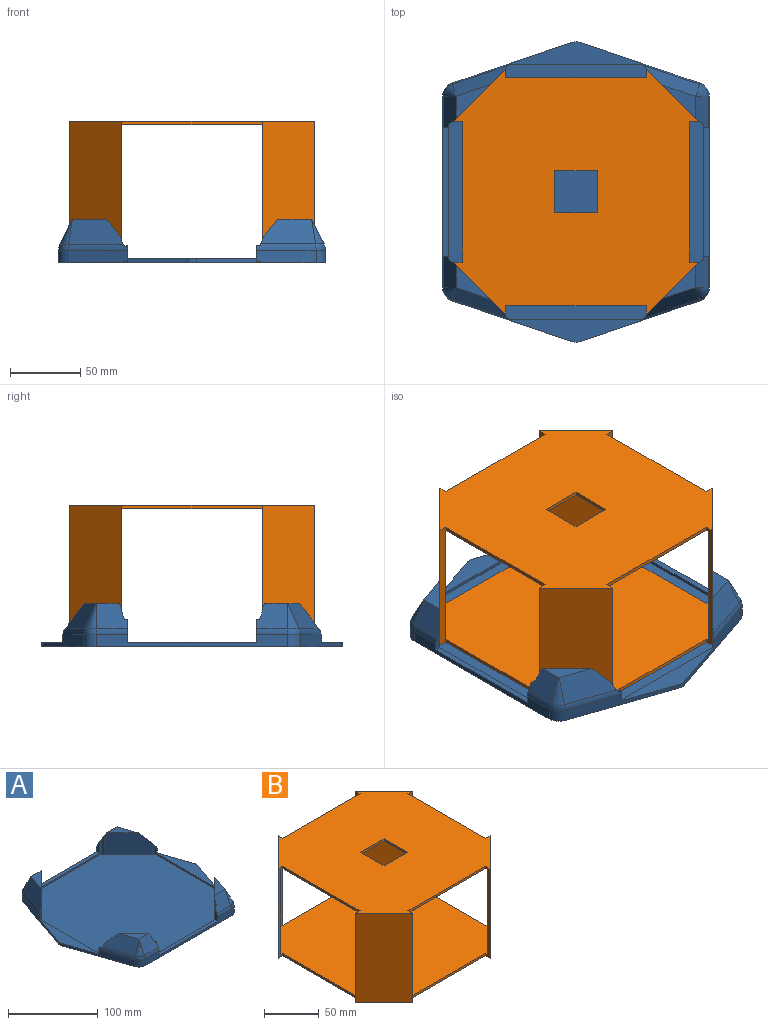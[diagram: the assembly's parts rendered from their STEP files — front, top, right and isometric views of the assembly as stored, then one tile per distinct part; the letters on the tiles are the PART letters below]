
ASSEMBLY  parts=2 mates=1
PART A: 70 faces, bbox 213.9x190x31 mm
  f0: plane 182x182mm, normal (0,0,1), area 29110.5mm2, adj f20,f21,f22,f23,f24,f25,f26,f27
  f1: plane 85x29.08mm, normal (-0.95,0.32,0), area 531.7mm2, adj f7,f14,f35,f40,f45,f67
  f2: plane 135.7x8.69mm, normal (0,1,0), area 672.4mm2, adj f7,f15,f17,f37,f40,f41,f66,f69
  f3: plane 85x29.08mm, normal (0.95,0.32,0), area 531.7mm2, adj f7,f18,f39,f41,f42,f64
  f4: plane 85x29.08mm, normal (0.95,-0.32,0), area 544.3mm2, adj f7,f11,f39,f42,f43,f63
  f5: plane 135.7x8.97mm, normal (0,-1,0), area 684.7mm2, adj f7,f8,f12,f33,f43,f44,f60,f61
  f6: plane 85x29.08mm, normal (-0.95,-0.32,0), area 544.3mm2, adj f7,f9,f35,f44,f45,f58
  f7: plane 213.86x190mm, normal (0,0,-1), area 34634.8mm2, adj f1,f2,f3,f4,f5,f6,f40,f41
  f8: plane 16.04x4mm, normal (1,0,0), area 48mm2, adj f5,f28,f33,f54,f60
  f9: plane 9.52x0.76mm, normal (0,1,0), area 6.3mm2, adj f6,f26,f35,f58
  f10: plane 24.1x24.1mm, normal (0,0,1), area 191mm2, adj f27,f52,f54
  f11: plane 9.52x0.76mm, normal (0,1,0), area 6.3mm2, adj f4,f31,f39,f63
  f12: plane 16.04x4mm, normal (-1,0,0), area 48mm2, adj f5,f29,f33,f57,f61
  f13: plane 24.1x24.1mm, normal (0,0,1), area 191mm2, adj f30,f55,f57
  f14: plane 9.24x0.76mm, normal (0,-1,0), area 6.1mm2, adj f1,f25,f35,f67
  f15: plane 16.02x4mm, normal (1,0,0), area 47.3mm2, adj f2,f23,f37,f46,f69
  f16: plane 24.73x24.73mm, normal (0,0,1), area 201.2mm2, adj f24,f46,f47,f48
  f17: plane 16.02x4mm, normal (-1,0,0), area 47.3mm2, adj f2,f22,f37,f49,f66
  f18: plane 9.24x0.76mm, normal (0,-1,0), area 6.1mm2, adj f3,f20,f39,f64
  f19: plane 24.73x24.73mm, normal (0,0,1), area 201.2mm2, adj f21,f49,f50,f51
  f20: cylinder r=4mm len=16.59mm, axis (0,0,1), area 78.8mm2, adj f0,f18,f21,f38,f51,f64
  f21: plane 37x37mm, normal (-0.71,-0.71,0), area 1465.6mm2, adj f0,f19,f20,f22,f49,f51
  f22: cylinder r=4mm len=26.4mm, axis (0,0,1), area 133.1mm2, adj f0,f17,f21,f36,f49
  f23: cylinder r=4mm len=26.4mm, axis (0,0,1), area 133.1mm2, adj f0,f15,f24,f36,f46
  f24: plane 37x37mm, normal (0.71,-0.71,0), area 1465.6mm2, adj f0,f16,f23,f25,f46,f48
  f25: cylinder r=4mm len=16.59mm, axis (0,0,1), area 78.8mm2, adj f0,f14,f24,f34,f48,f67
  f26: cylinder r=4mm len=16.68mm, axis (0,0,1), area 80.4mm2, adj f0,f9,f27,f34,f52,f58
  f27: plane 37x37mm, normal (0.71,0.71,0), area 1461.5mm2, adj f0,f10,f26,f28,f52,f54
  f28: cylinder r=4mm len=26.07mm, axis (0,0,1), area 132.4mm2, adj f0,f8,f27,f32,f54
  f29: cylinder r=4mm len=26.07mm, axis (0,0,1), area 132.4mm2, adj f0,f12,f30,f32,f57
  f30: plane 37x37mm, normal (-0.71,0.71,0), area 1461.5mm2, adj f0,f13,f29,f31,f55,f57
  f31: cylinder r=4mm len=16.68mm, axis (0,0,1), area 80.4mm2, adj f0,f11,f30,f38,f55,f63
  f32: plane 92x2.18mm, normal (0,1,0), area 200.6mm2, adj f0,f28,f29,f33
  f33: plane 92x4mm, normal (0,0,1), area 368mm2, adj f5,f8,f12,f32
  f34: plane 92x2.18mm, normal (1,0,0), area 200.6mm2, adj f0,f25,f26,f35
  f35: plane 92x15.93mm, normal (0,0,1), area 792.9mm2, adj f1,f6,f9,f14,f34,f45
  f36: plane 92x2.18mm, normal (0,-1,0), area 200.6mm2, adj f0,f22,f23,f37
  f37: plane 92x4mm, normal (0,0,1), area 368mm2, adj f2,f15,f17,f36
  f38: plane 92x2.18mm, normal (-1,0,0), area 200.6mm2, adj f0,f20,f31,f39
  f39: plane 92x15.93mm, normal (0,0,1), area 792.9mm2, adj f3,f4,f11,f18,f38,f42
  f40: cylinder r=10mm len=9.46mm, axis (0,0,-1), area 107.9mm2, adj f1,f2,f7,f68
  f41: cylinder r=10mm len=9.46mm, axis (0,0,-1), area 107.9mm2, adj f2,f3,f7,f65
  f42: cylinder r=10mm len=6.47mm, axis (0,0,1), area 21mm2, adj f3,f4,f7,f39
  f43: cylinder r=10mm len=9.46mm, axis (0,0,-1), area 111.4mm2, adj f4,f5,f7,f62
  f44: cylinder r=10mm len=9.46mm, axis (0,0,-1), area 111.4mm2, adj f5,f6,f7,f59
  f45: cylinder r=10mm len=6.47mm, axis (0,0,1), area 21mm2, adj f1,f6,f7,f35
  f46: plane 21.85x17.93mm, normal (0,0.9,0.44), area 387.6mm2, adj f15,f16,f23,f24,f47,f69
  f47: cone r=0.25mm half-angle=26deg, axis (0,0,-1), area 114.3mm2, adj f16,f46,f48,f68
  f48: plane 38.94x21.59mm, normal (-0.85,0.29,0.44), area 687.9mm2, adj f16,f24,f25,f47,f67
  f49: plane 21.85x17.93mm, normal (0,0.9,0.44), area 387.6mm2, adj f17,f19,f21,f22,f50,f66
  f50: cone r=0.25mm half-angle=26deg, axis (0,0,-1), area 114.3mm2, adj f19,f49,f51,f65
  f51: plane 38.94x21.59mm, normal (0.85,0.29,0.44), area 687.9mm2, adj f19,f20,f21,f50,f64
  f52: plane 38.81x21.71mm, normal (-0.84,-0.29,0.45), area 671.1mm2, adj f10,f26,f27,f53,f58
  f53: cone r=10mm half-angle=27deg, axis (0,0,-1), area 108.5mm2, adj f52,f54,f59
  f54: plane 21.85x17.49mm, normal (0,-0.89,0.45), area 379.2mm2, adj f8,f10,f27,f28,f53,f60
  f55: plane 38.81x21.71mm, normal (0.84,-0.29,0.45), area 671.1mm2, adj f13,f30,f31,f56,f63
  f56: cone r=10mm half-angle=27deg, axis (0,0,-1), area 108.5mm2, adj f55,f57,f62
  f57: plane 21.85x17.49mm, normal (0,-0.89,0.45), area 379.2mm2, adj f12,f13,f29,f30,f56,f61
  f58: cylinder r=10mm len=42.59mm, axis (0.32,-0.95,0), area 206.1mm2, adj f6,f9,f26,f52,f59
  f59: sphere r=10mm, area 56.3mm2, adj f44,f53,f58,f60
  f60: cylinder r=10mm len=21.85mm, axis (1,0,0), area 103mm2, adj f5,f8,f54,f59
  f61: cylinder r=10mm len=21.85mm, axis (1,0,0), area 103mm2, adj f5,f12,f57,f62
  f62: sphere r=10mm, area 56.3mm2, adj f43,f56,f61,f63
  f63: cylinder r=10mm len=42.59mm, axis (0.32,0.95,0), area 206.1mm2, adj f4,f11,f31,f55,f62
  f64: cylinder r=10mm len=42.56mm, axis (-0.32,0.95,0), area 198.9mm2, adj f3,f18,f20,f51,f65
  f65: sphere r=10mm, area 54.4mm2, adj f41,f50,f64,f66
  f66: cylinder r=10mm len=21.85mm, axis (-1,0,0), area 99.2mm2, adj f2,f17,f49,f65
  f67: cylinder r=10mm len=42.56mm, axis (-0.32,-0.95,0), area 198.9mm2, adj f1,f14,f25,f48,f68
  f68: sphere r=10mm, area 54.4mm2, adj f40,f47,f67,f69
  f69: cylinder r=10mm len=21.85mm, axis (-1,0,0), area 99.2mm2, adj f2,f15,f46,f68
PART B: 38 faces, bbox 174x174x100 mm
  f0: plane 174x174mm, normal (0,0,-1), area 24238mm2, adj f8,f9,f10,f11,f12,f13,f14,f18
  f1: plane 174x174mm, normal (0,0,1), area 24238mm2, adj f7,f8,f9,f10,f11,f12,f13,f18
  f2: plane 166.93x164.46mm, normal (0,0,1), area 23733.7mm2, adj f4,f5,f6,f14,f15,f16,f17,f18
  f3: plane 166.93x164.46mm, normal (0,0,-1), area 23733.7mm2, adj f4,f5,f6,f7,f15,f16,f17,f18
  f4: plane 95x31mm, normal (0.71,-0.71,0), area 4164.9mm2, adj f2,f3,f15,f26
  f5: plane 95x33.46mm, normal (0.71,0.71,0), area 4496mm2, adj f2,f3,f22,f27
  f6: plane 95x33.46mm, normal (-0.71,0.71,0), area 4496mm2, adj f2,f3,f21,f23
  f7: plane 100x2.5mm, normal (0,1,0), area 250mm2, adj f1,f3,f8,f13
  f8: plane 100x6mm, normal (1,0,0), area 600mm2, adj f0,f1,f7,f9,f14,f15
  f9: plane 100x37mm, normal (-0.71,0.71,0), area 5232.6mm2, adj f0,f1,f8,f26
  f10: plane 100x37mm, normal (-0.71,-0.71,0), area 5232.6mm2, adj f0,f1,f22,f27
  f11: plane 100x37mm, normal (0.71,-0.71,0), area 5232.6mm2, adj f0,f1,f21,f23
  f12: plane 100x37mm, normal (0.71,0.71,0), area 5232.6mm2, adj f0,f1,f13,f18
  f13: plane 100x6mm, normal (-1,0,0), area 600mm2, adj f0,f1,f7,f12,f14,f17
  f14: plane 100x2.5mm, normal (0,1,0), area 250mm2, adj f0,f2,f8,f13
  f15: plane 95x2.46mm, normal (0,-1,0), area 234.1mm2, adj f2,f3,f4,f8
  f16: plane 95x31mm, normal (-0.71,-0.71,0), area 4164.9mm2, adj f2,f3,f17,f18
  f17: plane 95x2.46mm, normal (0,-1,0), area 234.1mm2, adj f2,f3,f13,f16
  f18: plane 100x6mm, normal (0,-1,0), area 365.9mm2, adj f0,f1,f2,f3,f12,f16,f19,f20
  f19: plane 100x2.5mm, normal (1,0,0), area 250mm2, adj f0,f2,f18,f21
  f20: plane 100x2.5mm, normal (1,0,0), area 250mm2, adj f1,f3,f18,f21
  f21: plane 100x6mm, normal (0,1,0), area 365.9mm2, adj f0,f1,f2,f3,f6,f11,f19,f20
  f22: plane 100x6mm, normal (1,0,0), area 365.9mm2, adj f0,f1,f2,f3,f5,f10,f24,f25
  f23: plane 100x6mm, normal (-1,0,0), area 365.9mm2, adj f0,f1,f2,f3,f6,f11,f24,f25
  f24: plane 100x2.5mm, normal (0,-1,0), area 250mm2, adj f0,f2,f22,f23
  f25: plane 100x2.5mm, normal (0,-1,0), area 250mm2, adj f1,f3,f22,f23
  f26: plane 100x6mm, normal (0,-1,0), area 365.9mm2, adj f0,f1,f2,f3,f4,f9,f28,f29
  f27: plane 100x6mm, normal (0,1,0), area 365.9mm2, adj f0,f1,f2,f3,f5,f10,f28,f29
  f28: plane 100x2.5mm, normal (-1,0,0), area 250mm2, adj f0,f2,f26,f27
  f29: plane 100x2.5mm, normal (-1,0,0), area 250mm2, adj f1,f3,f26,f27
  f30: plane 30x2.5mm, normal (-1,0,0), area 75mm2, adj f1,f3,f31,f33
  f31: plane 30x2.5mm, normal (0,-1,0), area 75mm2, adj f1,f3,f30,f32
  f32: plane 30x2.5mm, normal (1,0,0), area 75mm2, adj f1,f3,f31,f33
  f33: plane 30x2.5mm, normal (0,1,0), area 75mm2, adj f1,f3,f30,f32
  f34: plane 30x2.5mm, normal (0,1,0), area 75mm2, adj f0,f2,f35,f37
  f35: plane 30x2.5mm, normal (1,0,0), area 75mm2, adj f0,f2,f34,f36
  f36: plane 30x2.5mm, normal (0,-1,0), area 75mm2, adj f0,f2,f35,f37
  f37: plane 30x2.5mm, normal (-1,0,0), area 75mm2, adj f0,f2,f34,f36
PLACE A rot(axis=(0,0,1),90deg) t=(604.85,43.48,-87.88)mm
PLACE B rot(axis=(0.71,-0.71,0),180deg) t=(604.85,43.48,-86.88)mm
MATE fastened A.f0 <-> B.f1  axis (0,0,1) through (604.85,43.48,-136.88)mm
